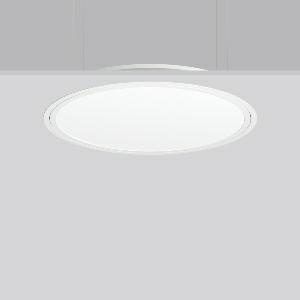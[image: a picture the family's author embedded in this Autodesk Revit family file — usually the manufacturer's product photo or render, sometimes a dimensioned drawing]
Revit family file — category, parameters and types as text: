
# Revit family: triona_round_e_312383_002_1_12_f276
name_source: partatom
category: Lighting Fixtures
units: mm (PartAtom-declared; Revit-internal decimal feet)

## family parameters
Cut with Voids When Loaded = No
Host = Face
Light Source = No
Part Type = Normal
Room Calculation Point = No
Round Connector Dimension = Use Diameter
Shared = No

## types (1)
- TRIONA round E (1 x LED Modul 840, 6750 lm, 4000)
    Apparent Load = 70 VA
    CIE Flux Codes = 49 80 96 100 100
    Color Rendering = 80
    Color Temperature = 4000
    Default Elevation = 1800 mm
    Description = Series: TRIONA round
Decorative round LED recessed surface luminaire. Cover made of sheet steel, powder-coated. Frame made of aluminium, powder-coated. Recessed ring: aluminium extrusion profile, powder coated. Light emission through a diffuser: plastic, opal. Lightguide and diffuser made of non-yellowing plastic (PMMA). Lateral light emission (RZB SIDELITE technology) for above-average homogeneous light distribution. Suitable for installation in cavity ceilings. Tool-free mounting system thanks to the rocker arm mechanism (patent pending). Electronic ballast included. Very easy installation thanks to Plug+Play connection. 
Colour: traffic white, matt (RAL 9016)
Diameter: 725 mm
Height: 2 mm
Cut-out diameter: 702 mm
Recess height: 100 mm
Luminaire: recess height: 89 mm
Lamp: LED
Socket: without socket
Colour temperature: 4000K
Colour rendering index (CRI): 80
System power: 70 W
Rated luminous flux: 6750 lm
Luminous efficiency: 96 lm/W
Control gear: Converter, dimmable, DALI
Protection class: I
Type of protection: IP 40
    Height = 0 mm  [stored 0 ft]
    Lamp = 1 x LED Modul 840
    Lamp Light Flux = 6750 lm
    Lamp count = 1
    Length = 725 mm
    Lifetime = 50000 h
    Luminous efficacy = 96 lm/W
    Manufacturer = RZB
    ModVariant = No
    Model = 312383.002.1.12
    Mounting Place = Ceiling
    Mounting Type = Recessed
    Number of Poles = 1
    OnlyDefault = Yes
    Power Factor = 1
    Product Name = TRIONA round E
    Product group = Recessed modular luminaires
    ProductGroupID = 406
    Protection Class = Protection class I
    Protection Degree = IP 20
    RLX_Detail_Level = 1
    RLX_Emergency_Light_Flux = 0 lm
    RLX_Emergency_Type = 0
    RLX_Emergency_Type_DB = No
    RlxData = <blob elided: 34517 chars, md5=5501522b>
    Socket = socket
    Standby Power = 0 W
    System Light Flux = 6750 lm
    System Power = 70 W
    Type Comments = Product without accessories
    Type Image = 312383.002.12.jpg
    URL = http://relux.com
    VarID = ---
    Voltage = 230 V
    Voltage Range = 220-240 V
    Weight = 0.00 kg
    Width = 0 mm  [stored 0 ft]

note: [stored X ft] marks values corroborated as IEEE doubles in the binary element streams (Revit-internal decimal feet)

## geometry (parser evidence)
native form markers: Blend x4, Sweep x10
no freeform markers — native parametric forms only
